# Revit family: Sink_Himacs_CS490D
name_source: partatom
category: Plumbing Fixtures
revit_build: Autodesk Revit Architecture 2014 (Build: 20131024_2115(x64)
units: mm (PartAtom-declared; Revit-internal decimal feet)

## types (1)
- Sink_Himacs_CS490D
    BIMobject category = Sanitary
    Date of publishing = 2014-10-09
    Depth = 420 mm  [stored 1.37795 ft]
    Design country = Italy
    Edition number = 1
    Height = 210 mm  [stored 0.688976 ft]
    IFC Classification = Furnishing Element
    Installation instructions = http://himacs.eu
    Manufacturer country = Italy
    Manufacturer name = HI-MACS
    Material Main = Natural Acrylic stone_Himacs_CS449RS_White
    Material Secondary = Steel_Himacs_CS490D_Polished
    NBS Reference Code = 35-65-70-94
    NBS Reference Description = Wash Basin Systems
    Nominal height = 196
    Nominal width = 540
    Product SKU = CS490D
    Product data url = http://himacs.bimobject.com
    Product family = Sinks, Baby Baths & Bowls
    Product group = Sinks
    QR code = http://himacs.bimobject.com
    Technical description = http://himacs.eu
    UNSPSC Code = 301815
    Uniclass 1.4 Code = L7212
    Uniclass 1.4 Description = Washbasins
    Uniclass 2.0 Code = SS-35-65-70-94
    Uniclass 2.0 Description = Wash Basin Systems
    Weight Net (Kg) = 10,7
    Width = 540 mm  [stored 1.77165 ft]

note: [stored X ft] marks values corroborated as IEEE doubles in the binary element streams (Revit-internal decimal feet)

## geometry (parser evidence)
native form markers: Blend x4, Sweep x5
no freeform markers — native parametric forms only
